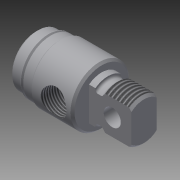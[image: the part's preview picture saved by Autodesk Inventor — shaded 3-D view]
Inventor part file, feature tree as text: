
AUTODESK INVENTOR PART (.ipt)
format: ipt  version: 2014 SP2 (Build 180246200, 246)  size: 302,080 bytes
history: native  units: in
note: dims shown in document units (in); Inventor stores cm internally (conversion verified against a paired STEP export)
features: other x154, sketch x7, revolve x4, thread x2, extrude x2, hole x1
ambient origin geometry x8: Origin, YZ Plane, XZ Plane, XY Plane, X Axis, Y Axis, Z Axis, Center Point
bodies: Solid1 (feature_tree)
feature tree (170):
  revolve  "Revolution1"  Angle=360.0deg
  revolve  "Revolution2"  [1 undecoded]
  thread  "Thread1"  [1 undecoded]
  extrude  "Extrusion1"  TaperAngle=360.0deg  [1 undecoded]
  hole  "Hole1"  [1 undecoded]
  revolve  "Revolution3"  [1 undecoded]
  thread  "Thread2"  [1 undecoded]
  revolve  "Revolution4"  [1 undecoded]
  extrude  "Extrusion2"  [1 undecoded]
  other  "1_XY"
  other  "1_YZ"
  other  "1_ZX"
  other  "1_X"
  other  "1_Y"
  other  "1_Z"
  other  "1_Center"
  other  "c1_XY"
  other  "c1_YZ"
  other  "c1_ZX"
  other  "c1_X"
  other  "c1_Y"
  other  "c1_Z"
  other  "c1_Center"
  other  "c2_XY"
  other  "c2_YZ"
  other  "c2_ZX"
  other  "c2_X"
  other  "c2_Y"
  other  "c2_Z"
  other  "c2_Center"
  other  "cc1_XY"
  other  "cc1_YZ"
  other  "cc1_ZX"
  other  "cc1_X"
  other  "cc1_Y"
  other  "cc1_Z"
  other  "cc1_Center"
  other  "cc2_XY"
  other  "cc2_YZ"
  other  "cc2_ZX"
  other  "cc2_X"
  other  "cc2_Y"
  other  "cc2_Z"
  other  "cc2_Center"
  other  "lovra1_XY"
  other  "lovra1_YZ"
  other  "lovra1_ZX"
  other  "lovra1_X"
  other  "lovra1_Y"
  other  "lovra1_Z"
  other  "lovra1_Center"
  other  "lovra2_XY"
  other  "lovra2_YZ"
  other  "lovra2_ZX"
  other  "lovra2_X"
  other  "lovra2_Y"
  other  "lovra2_Z"
  other  "lovra2_Center"
  other  "lovra21_XY"
  other  "lovra21_YZ"
  other  "lovra21_ZX"
  other  "lovra21_X"
  other  "lovra21_Y"
  other  "lovra21_Z"
  other  "lovra21_Center"
  other  "lovra22_XY"
  other  "lovra22_YZ"
  other  "lovra22_ZX"
  other  "lovra22_X"
  other  "lovra22_Y"
  other  "lovra22_Z"
  other  "lovra22_Center"
  other  "lovra3_XY"
  other  "lovra3_YZ"
  other  "lovra3_ZX"
  other  "lovra3_X"
  other  "lovra3_Y"
  other  "lovra3_Z"
  other  "lovra3_Center"
  other  "olen_XY"
  other  "olen_YZ"
  other  "olen_ZX"
  other  "olen_X"
  other  "olen_Y"
  other  "olen_Z"
  other  "olen_Center"
  other  "p1_XY"
  other  "p1_YZ"
  other  "p1_ZX"
  other  "p1_X"
  other  "p1_Y"
  other  "p1_Z"
  other  "p1_Center"
  other  "p2_XY"
  other  "p2_YZ"
  other  "p2_ZX"
  other  "p2_X"
  other  "p2_Y"
  other  "p2_Z"
  other  "p2_Center"
  other  "port_XY"
  other  "port_YZ"
  other  "port_ZX"
  other  "port_X"
  other  "port_Y"
  other  "port_Z"
  other  "port_Center"
  other  "port2_XY"
  other  "port2_YZ"
  other  "port2_ZX"
  other  "port2_X"
  other  "port2_Y"
  other  "port2_Z"
  other  "port2_Center"
  other  "thd1_XY"
  other  "thd1_YZ"
  other  "thd1_ZX"
  other  "thd1_X"
  other  "thd1_Y"
  other  "thd1_Z"
  other  "thd1_Center"
  other  "thd2_XY"
  other  "thd2_YZ"
  other  "thd2_ZX"
  other  "thd2_X"
  other  "thd2_Y"
  other  "thd2_Z"
  other  "thd2_Center"
  other  "to_mounting_bracket_XY"
  other  "to_mounting_bracket_YZ"
  other  "to_mounting_bracket_ZX"
  other  "to_mounting_bracket_X"
  other  "to_mounting_bracket_Y"
  other  "to_mounting_bracket_Z"
  other  "to_mounting_bracket_Center"
  other  "to_nut_XY"
  other  "to_nut_YZ"
  other  "to_nut_ZX"
  other  "to_nut_X"
  other  "to_nut_Y"
  other  "to_nut_Z"
  other  "to_nut_Center"
  other  "to_pin_XY"
  other  "to_pin_YZ"
  other  "to_pin_ZX"
  other  "to_pin_X"
  other  "to_pin_Y"
  other  "to_pin_Z"
  other  "to_pin_Center"
  other  "to_screw_XY"
  other  "to_screw_YZ"
  other  "to_screw_ZX"
  other  "to_screw_X"
  other  "to_screw_Y"
  other  "to_screw_Z"
  other  "to_screw_Center"
  other  "to_tube_XY"
  other  "to_tube_YZ"
  other  "to_tube_ZX"
  other  "to_tube_X"
  other  "to_tube_Y"
  other  "to_tube_Z"
  other  "to_tube_Center"
  sketch  "Sketch_8"  dims[d2=0.3547in d3=0.0in d4=0.625in d5=0.0in]
  sketch  "Sketch_15"  dims[d14=0.3021in d15=0.0in d16=360.0deg]
  sketch  "Sketch_9"  dims[d6=0.312in d7=0.75in d8=0.375in d9=0.25in d10=0.5635in d11=0.9284in d12=120.0deg d13=360.0deg]
  sketch  "Sketch4"  dims[d0=360.0deg d1=360.0deg]
  sketch  "Sketch_68"
  sketch  "Sketch_24"  dims[d17=0.5587in d18=0.0in]
  sketch  "Sketch_43"  dims[d19=0.0in d20=0.0in d21=0.0in d22=0.0in d23=0.0in d24=0.0in d25=0.0in d26=0.0in]
note: 8 required parameter values undecoded (feature->parameter linkage not recoverable at this tier; creation-order binding heuristic only, values carry confidence <= 0.55)